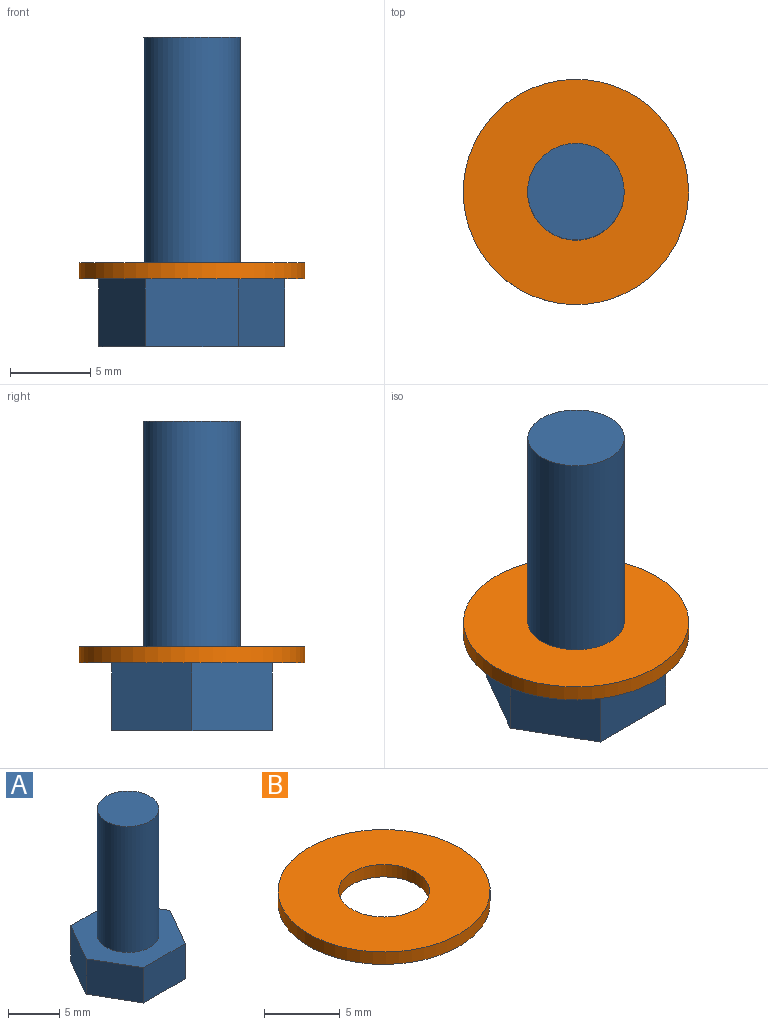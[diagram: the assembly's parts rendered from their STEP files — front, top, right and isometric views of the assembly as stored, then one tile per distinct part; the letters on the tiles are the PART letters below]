
ASSEMBLY  parts=2 mates=1
PART A: 10 faces, bbox 11.5x10x19.2 mm
  f0: plane 5.77x4.2mm, normal (0,1,0), area 24.2mm2, adj f1,f5,f6,f7
  f1: plane 5x4.2mm, normal (-0.87,0.5,0), area 24.2mm2, adj f0,f2,f6,f7
  f2: plane 5x4.2mm, normal (-0.87,-0.5,0), area 24.2mm2, adj f1,f3,f6,f7
  f3: plane 5.77x4.2mm, normal (0,-1,0), area 24.2mm2, adj f2,f4,f6,f7
  f4: plane 5x4.2mm, normal (0.87,-0.5,0), area 24.2mm2, adj f3,f5,f6,f7
  f5: plane 5x4.2mm, normal (0.87,0.5,0), area 24.2mm2, adj f0,f4,f6,f7
  f6: plane 11.55x10mm, normal (0,0,-1), area 86.6mm2, adj f0,f1,f2,f3,f4,f5
  f7: plane 11.55x10mm, normal (0,0,1), area 58.3mm2, adj f0,f1,f2,f3,f4,f5,f8
  f8: cylinder r=3mm len=15mm, axis (0,0,-1), area 282.7mm2, adj f7,f9
  f9: plane 6x6mm, normal (0,0,1), area 28.3mm2, adj f8
PART B: 4 faces, bbox 14x14x1 mm
  f0: cylinder r=3mm len=6mm, axis (0,0,-1), area 18.8mm2, adj f2,f3
  f1: cylinder r=7mm len=14mm, axis (0,0,-1), area 44mm2, adj f2,f3
  f2: plane 14x14mm, normal (0,0,1), area 125.7mm2, adj f0,f1
  f3: plane 14x14mm, normal (0,0,-1), area 125.7mm2, adj f0,f1
PLACE A t=(180,-37.08,-4)mm
PLACE B t=(180,22.92,-4)mm
MATE fastened B.f0 <-> A.f8  axis (0,0,-1) through (180,-37.08,-4)mm
